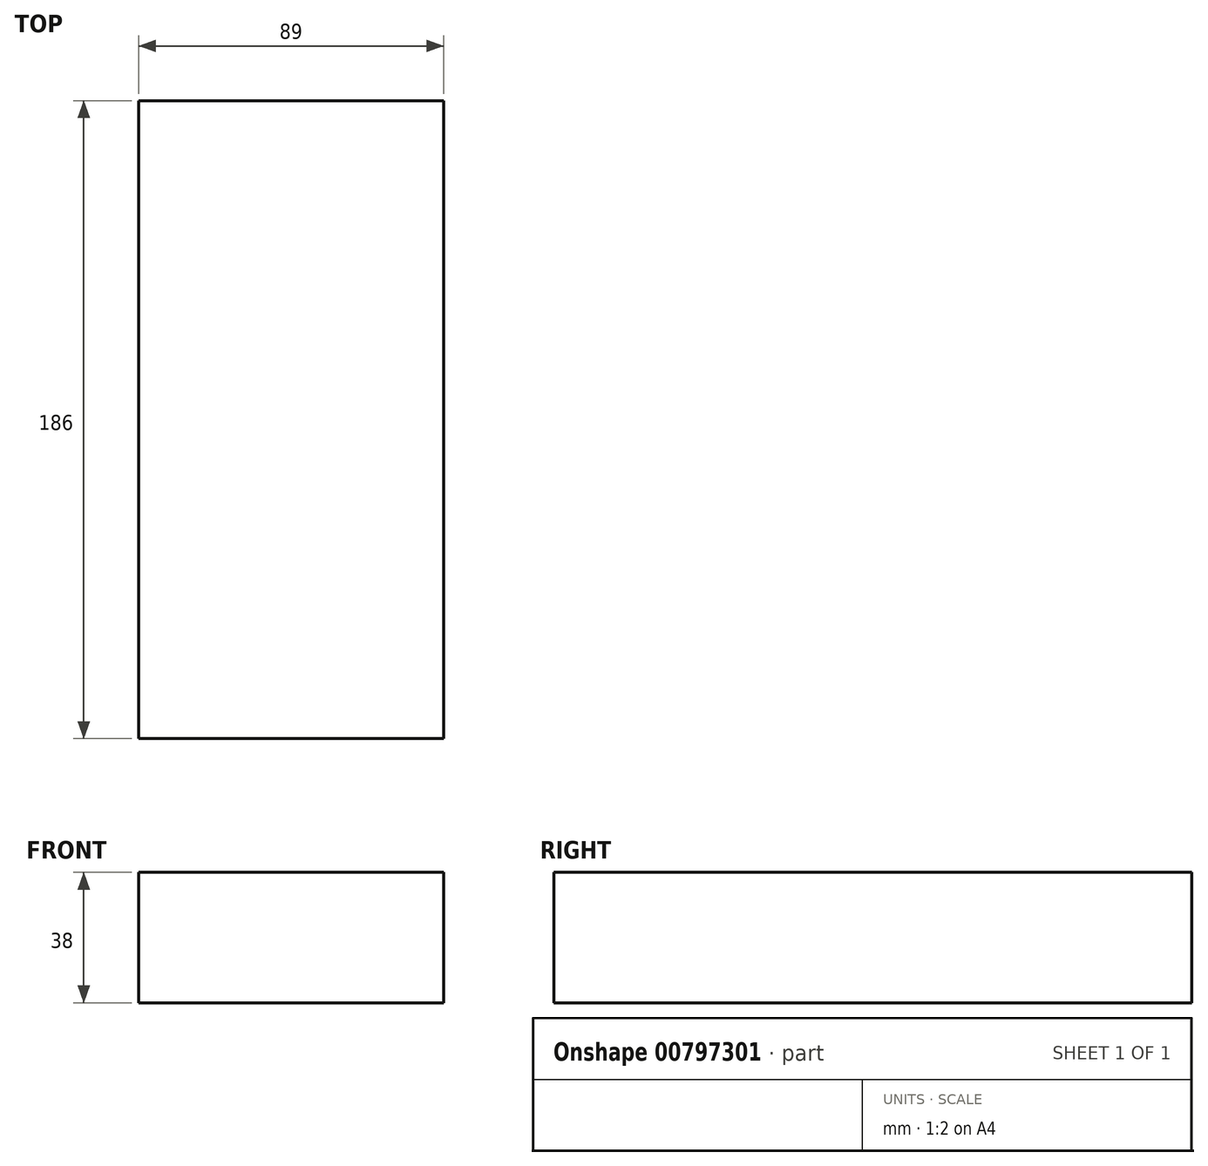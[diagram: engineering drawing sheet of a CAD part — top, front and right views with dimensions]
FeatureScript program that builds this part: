
annotation { "Feature Type Name" : "Feature", "Feature Type Description" : "" }
export const myFeature = defineFeature(function(context is Context, id is Id, definition is map)
    precondition{}
    {
        {
            var Q0;
            Q0=qCreatedBy(makeId("Front.planeOp"),FACE);
            var sketch = newSketch(context, id + "F0", { "sketchPlane" : qUnion([Q0])});
            skLineSegment(sketch, "E0.bottom", {"start": v(44.5, 19) * mm, "end": v(-44.5, 19) * mm});
            skLineSegment(sketch, "E0.top", {"start": v(44.5, -19) * mm, "end": v(-44.5, -19) * mm});
            skLineSegment(sketch, "E0.left", {"start": v(44.5, 19) * mm, "end": v(44.5, -19) * mm});
            skLineSegment(sketch, "E0.right", {"start": v(-44.5, 19) * mm, "end": v(-44.5, -19) * mm});
            skPoint(sketch, "E0.middle", {"position": v(0, 0) * mm});
            skSolve(sketch);
        }
        {
            var Q0;
            Q0 = qSketchRegion(id + "F0", true);
            extrude(context, id + "F1", {"entities" : qUnion([Q0]), "depth" : 186 * mm, "offsetDistance" : 25 * mm, "symmetric" : true});
        }
    });
